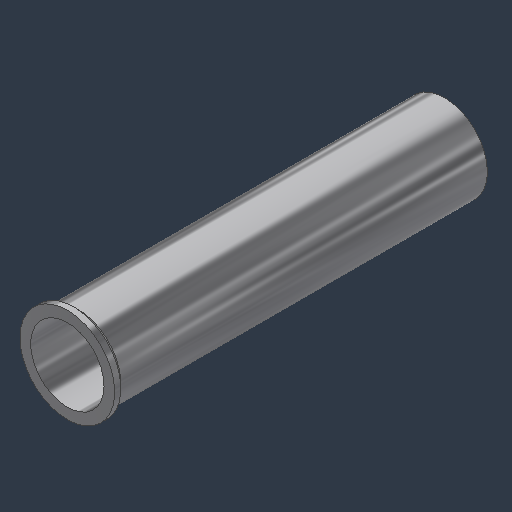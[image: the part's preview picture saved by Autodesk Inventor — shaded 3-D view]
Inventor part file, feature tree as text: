
AUTODESK INVENTOR PART (.ipt)
format: ipt  version: 2024.3 (Build 283343000, 343)  size: 148,480 bytes
history: native  units: mm (DEFAULTED — no unit token found)
features: extrude x2, sketch x2, chamfer x1
ambient origin geometry x8: Origin, YZ Plane, XZ Plane, XY Plane, X Axis, Y Axis, Z Axis, Center Point
bodies: Solid1 (feature_tree)
feature tree (5):
  extrude  "Extrusion1"  Depth=3.175mm
  extrude  "Extrusion2"  Depth=3.175mm
  chamfer  "Chamfer2"  Distance=3.175mm
  sketch  "Sketch2"  dims[d0=38.1mm d1=3.175mm]
  sketch  "Sketch3"  dims[d2=195.98mm d3=0.0mm d4=49.2mm d5=3.175mm d6=0.0mm d7=2.375mm d11=2.3749mm d12=3.175mm d13=45.0deg]
